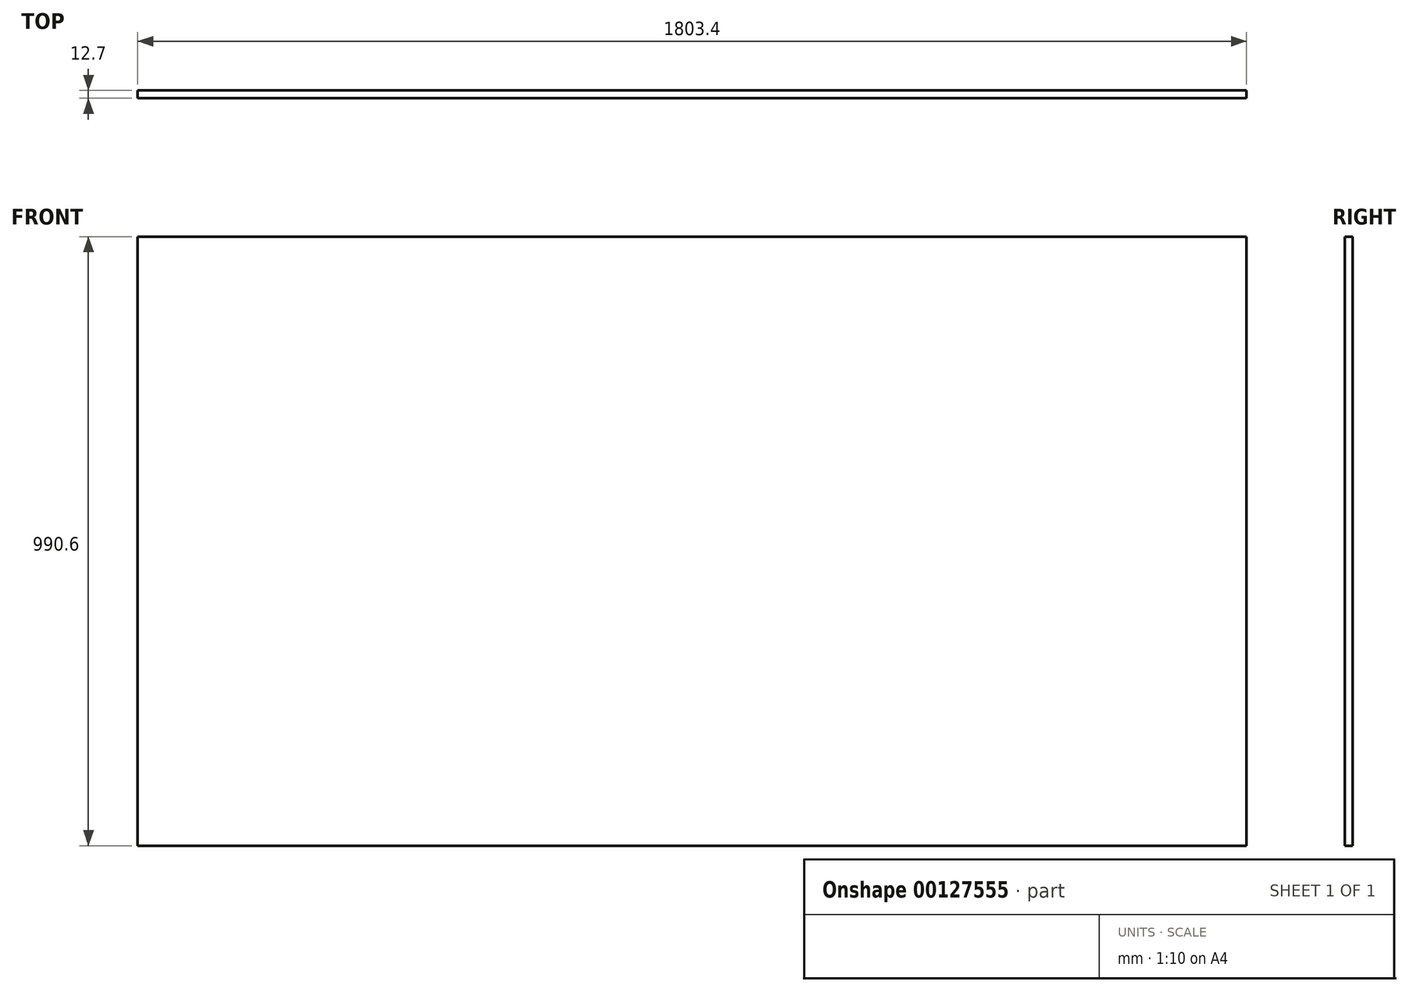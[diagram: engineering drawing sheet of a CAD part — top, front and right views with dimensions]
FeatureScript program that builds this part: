
annotation { "Feature Type Name" : "Feature", "Feature Type Description" : "" }
export const myFeature = defineFeature(function(context is Context, id is Id, definition is map)
    precondition{}
    {
        {
            var Q0;
            Q0=qCreatedBy(makeId("Front.planeOp"),FACE);
            var sketch = newSketch(context, id + "F0", { "sketchPlane" : qUnion([Q0])});
            skLineSegment(sketch, "E0.bottom", {"start": v(901.7, -495.3) * mm, "end": v(-901.7, -495.3) * mm});
            skLineSegment(sketch, "E0.top", {"start": v(901.7, 495.3) * mm, "end": v(-901.7, 495.3) * mm});
            skLineSegment(sketch, "E0.left", {"start": v(901.7, -495.3) * mm, "end": v(901.7, 495.3) * mm});
            skLineSegment(sketch, "E0.right", {"start": v(-901.7, -495.3) * mm, "end": v(-901.7, 495.3) * mm});
            skPoint(sketch, "E0.middle", {"position": v(0, 0) * mm});
            skSolve(sketch);
        }
        {
            var Q0;
            Q0=makeQuery(id+"F0.imprint","IMPRINT",FACE,{"disambiguationData":[TD([[makeQuery(id+"F0.imprint","IMPRINT",EDGE,{"derivedFrom":sQuery(id+"F0.wireOp",EDGE,"E0.bottom")}),-1.0]])]});
            extrude(context, id + "F1", {"entities" : qUnion([Q0]), "depth" : 12.7 * mm});
        }
    });
